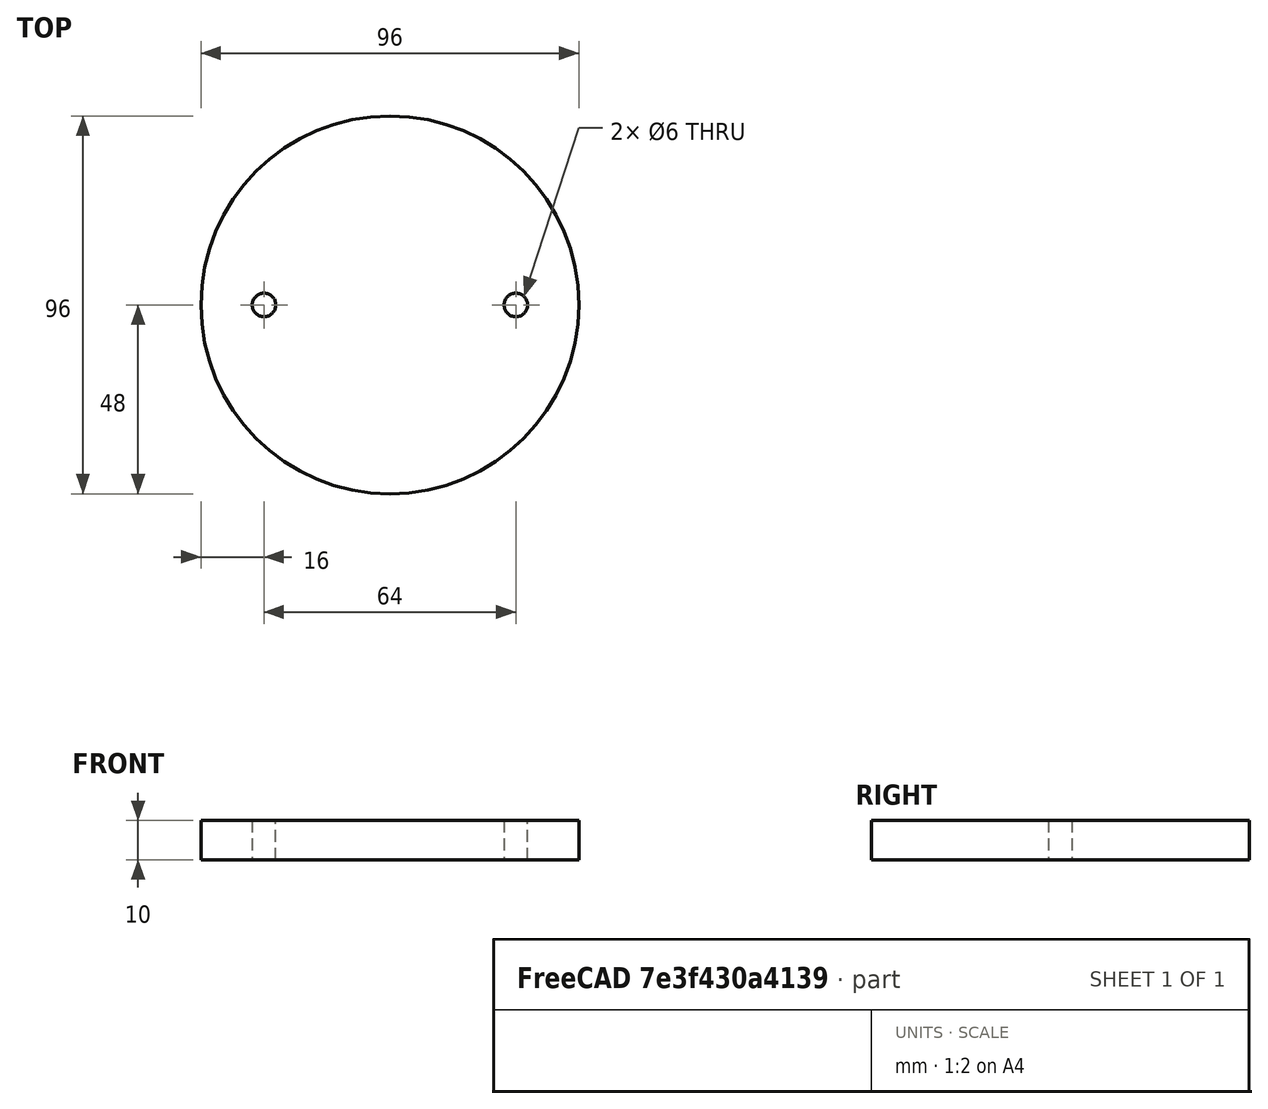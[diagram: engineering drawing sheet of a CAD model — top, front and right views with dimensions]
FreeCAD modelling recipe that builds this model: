
FCSTD DOCUMENT  (FreeCAD 1.1R14555 (Git shallow))
Label: bottom plate well
License: All rights reserved
LicenseURL: https://en.wikipedia.org/wiki/All_rights_reserved
objects: App::Point×1, Sketcher::SketchObject×1, PartDesign::Pad×1, PartDesign::Body×1
note: 6 computed .brp shape members not serialized (recipe doc carries the construction recipe); baked Part::Feature solids carry a one-line shape summary decoded from their .brp

FEATURE [App::Point] Origin001
  Role = Origin
FEATURE [Sketcher::SketchObject] Sketch
  ArcFitTolerance = 1e-06
  AttachmentSupport = -> [Origin]
  ExternalTypes = [0]
  FullyConstrained = true
  MakeInternals = false
  MapMode = 5
  sketch-geometry (3):
    g0: Circle CenterX=0 CenterY=0 CenterZ=0 NormalX=0 NormalY=0 NormalZ=1 AngleXU=0 Radius=48
    g1: Circle CenterX=-32 CenterY=0 CenterZ=0 NormalX=0 NormalY=0 NormalZ=1 AngleXU=0 Radius=3
    g2: Circle CenterX=32 CenterY=0 CenterZ=0 NormalX=0 NormalY=0 NormalZ=1 AngleXU=0 Radius=3
  constraints (8):
    c: Coincident(g0,g-1)
    c: Diameter(g0) = 96
    c: PointOnObject(g1,g-1)
    c: PointOnObject(g2,g-1)
    c: Equal(g1,g2)
    c: Diameter(g1) = 6
    c: DistanceX(g1,g0) = 32
    c: DistanceX(g0,g2) = 32
FEATURE [PartDesign::Pad] Pad
  Direction = (0,0,1)
  Length = 10
  Length2 = 10
  Profile = -> Sketch
  ReferenceAxis = -> Sketch [N_Axis]
  SideType = 0
  Suppressed = false
  Type = 0
  Type2 = 0
FEATURE [PartDesign::Body] Body
  AllowCompound = false
  Group = -> [Sketch,Pad]
  Origin = -> Origin
  Tip = -> Pad
